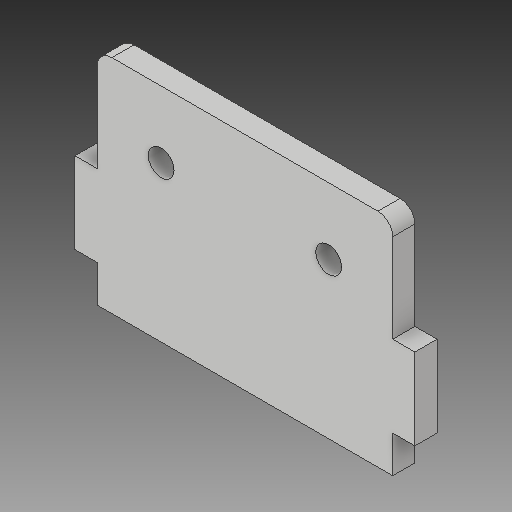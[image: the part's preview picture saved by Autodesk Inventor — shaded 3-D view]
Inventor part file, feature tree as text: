
AUTODESK INVENTOR PART (.ipt)
format: ipt  version: 2019 (Build 230136000, 136)  size: 124,416 bytes
history: native  units: mm
features: extrude x1, fillet x1
ambient origin geometry x8: Origin, YZ Plane, XZ Plane, XY Plane, X Axis, Y Axis, Z Axis, Center Point
bodies: Body1 (feature_tree)
feature tree (2):
  extrude  "Extrusion2"  Depth=60.0mm
  fillet  "Fillet3"  Radius=80.0mm
